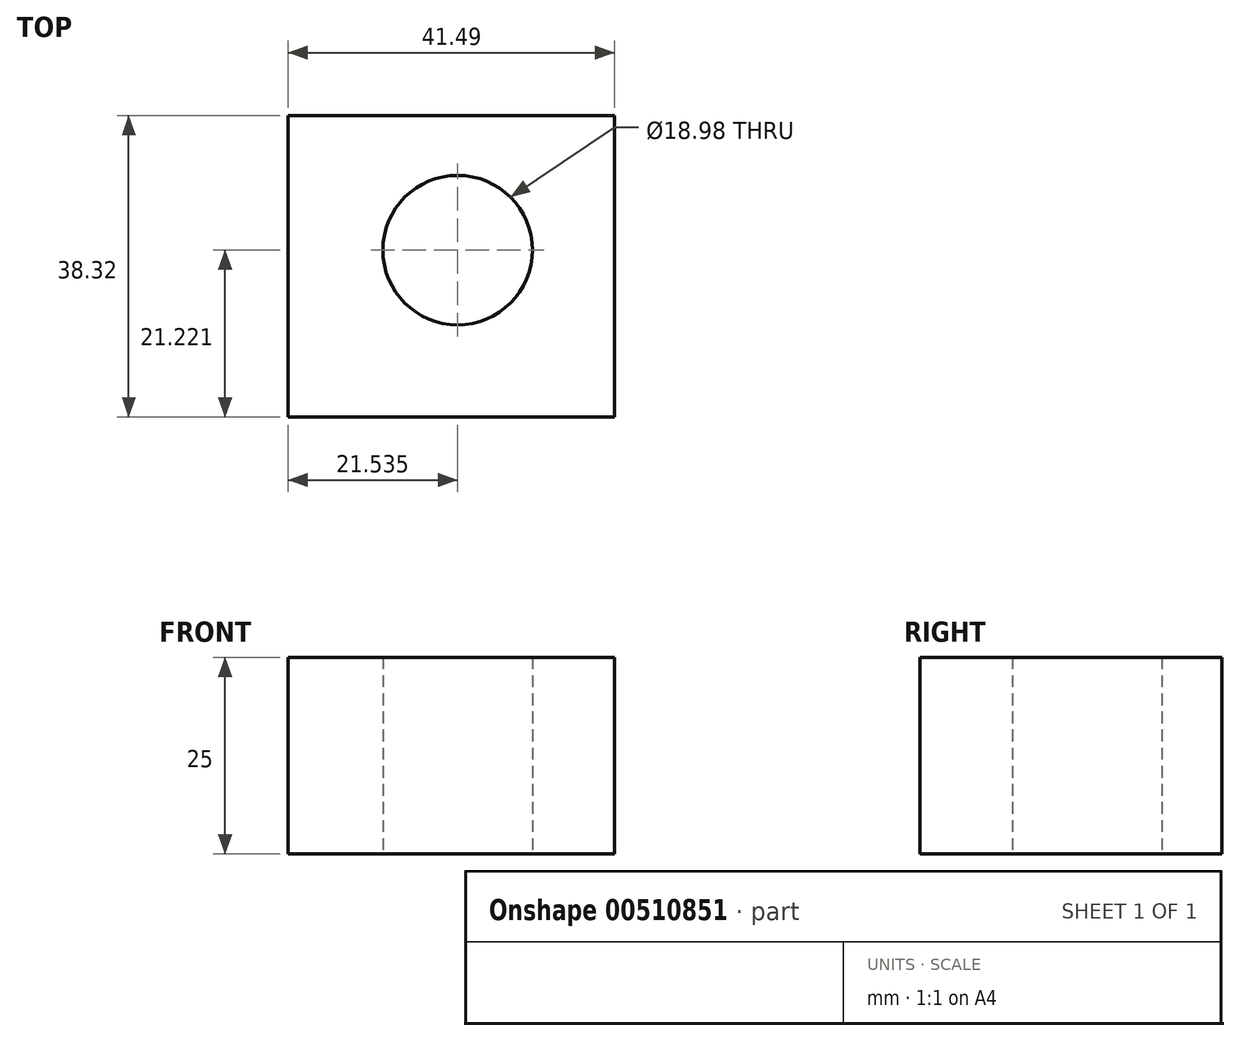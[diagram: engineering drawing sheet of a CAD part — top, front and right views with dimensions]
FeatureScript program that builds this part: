
annotation { "Feature Type Name" : "Feature", "Feature Type Description" : "" }
export const myFeature = defineFeature(function(context is Context, id is Id, definition is map)
    precondition{}
    {
        {
            var Q0;
            Q0=qCreatedBy(makeId("Top.planeOp"),FACE);
            var sketch = newSketch(context, id + "F0", { "sketchPlane" : qUnion([Q0])});
            skLineSegment(sketch, "E0.bottom", {"start": v(-41.5, 46.24) * mm, "end": v(0, 46.24) * mm});
            skLineSegment(sketch, "E0.top", {"start": v(-41.5, 7.92) * mm, "end": v(0, 7.92) * mm});
            skLineSegment(sketch, "E0.left", {"start": v(-41.5, 46.24) * mm, "end": v(-41.5, 7.92) * mm});
            skLineSegment(sketch, "E0.right", {"start": v(0, 46.24) * mm, "end": v(0, 7.92) * mm});
            skCircle(sketch, "E1", {"center": v(-19.95, 29.14) * mm, "radius": 9.5 * mm});
            skSolve(sketch);
        }
        {
            var Q0;
            Q0 = qSketchRegion(id + "F0", true);
            extrude(context, id + "F1", {"entities" : qUnion([Q0]), "depth" : 25 * mm});
        }
    });
